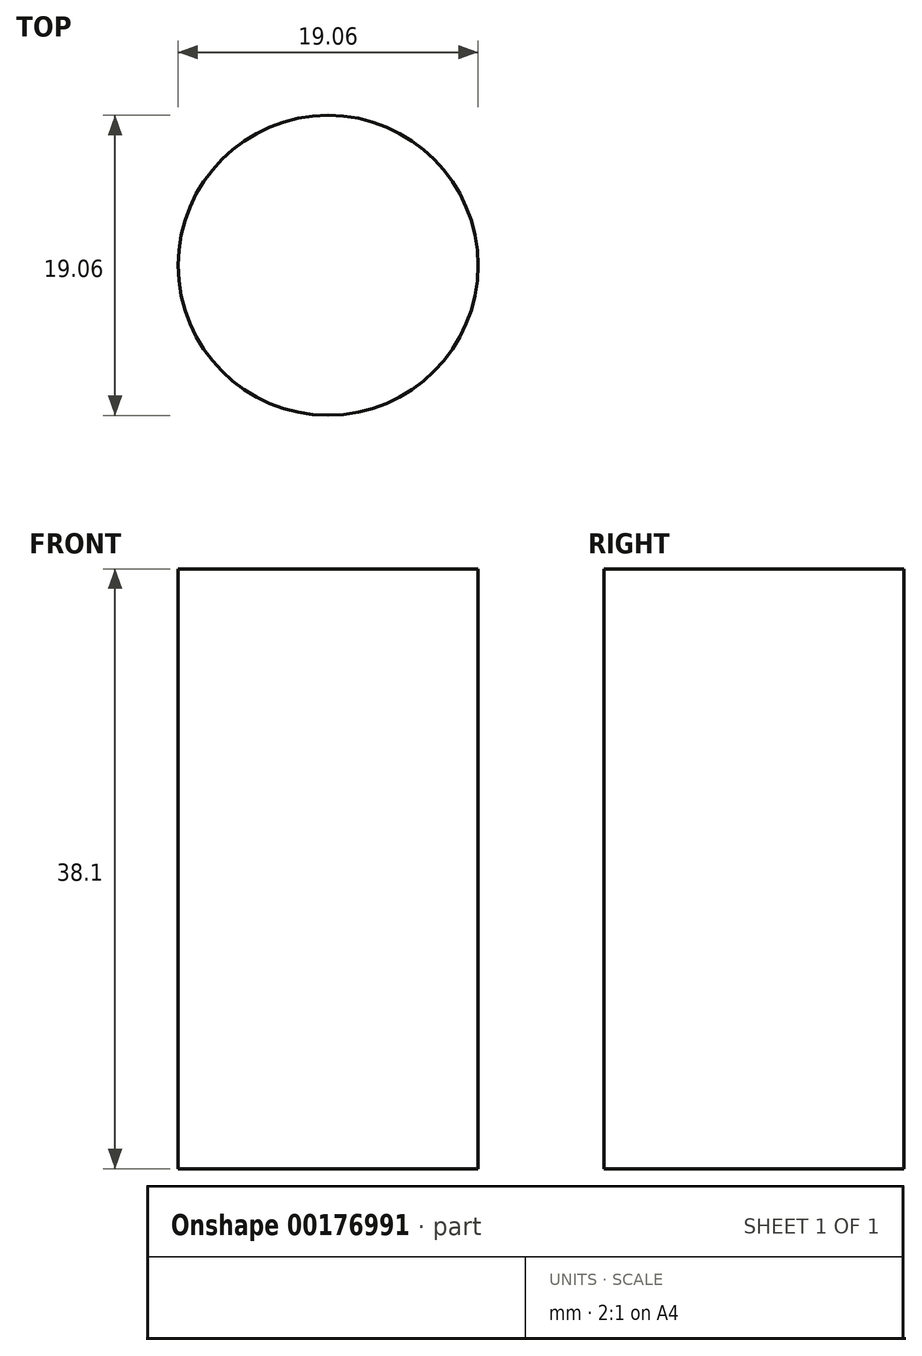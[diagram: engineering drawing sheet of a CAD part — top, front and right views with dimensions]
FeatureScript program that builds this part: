
annotation { "Feature Type Name" : "Feature", "Feature Type Description" : "" }
export const myFeature = defineFeature(function(context is Context, id is Id, definition is map)
    precondition{}
    {
        {
            var Q0;
            Q0=qCreatedBy(makeId("Top.planeOp"),FACE);
            var sketch = newSketch(context, id + "F0", { "sketchPlane" : qUnion([Q0])});
            skCircle(sketch, "E0", {"center": v(0, 0) * mm, "radius": 9.53 * mm});
            skSolve(sketch);
        }
        {
            var Q0;
            Q0 = qSketchRegion(id + "F0", true);
            extrude(context, id + "F1", {"entities" : qUnion([Q0]), "depth" : 38.1 * mm});
        }
    });
